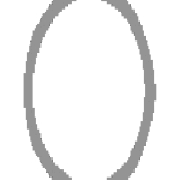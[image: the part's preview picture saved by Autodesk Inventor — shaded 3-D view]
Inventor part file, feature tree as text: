
AUTODESK INVENTOR PART (.ipt)
format: ipt  version: 2021 (Build 250183000, 183)  size: 161,280 bytes
history: native  units: in
note: dims shown in document units (in); Inventor stores cm internally (conversion verified against a paired STEP export)
features: other x5, sketch x2, sweep x1, plane x1
ambient origin geometry x8: Origin, YZ Plane, XZ Plane, XY Plane, X Axis, Y Axis, Z Axis, Center Point
bodies: Solid1 (feature_tree), Body (feature_tree)
feature tree (9):
  other  "Driven Length"
  other  "Frame Generator"
  other  "Start Plane"
  other  "End Plane"
  sweep  "Sweep Path"
  other  "Orientation Work Plane"
  sketch  "Sketch2"  dims[d0=1.0in d1=0.065in]
  plane  "Work Plane3"
  sketch  "Sketch3"  dims[d2=7.854in d4=-0.0in d5=7.854in d8=90.0deg d9=7.854in d10=0.0in d11=0.0in]
